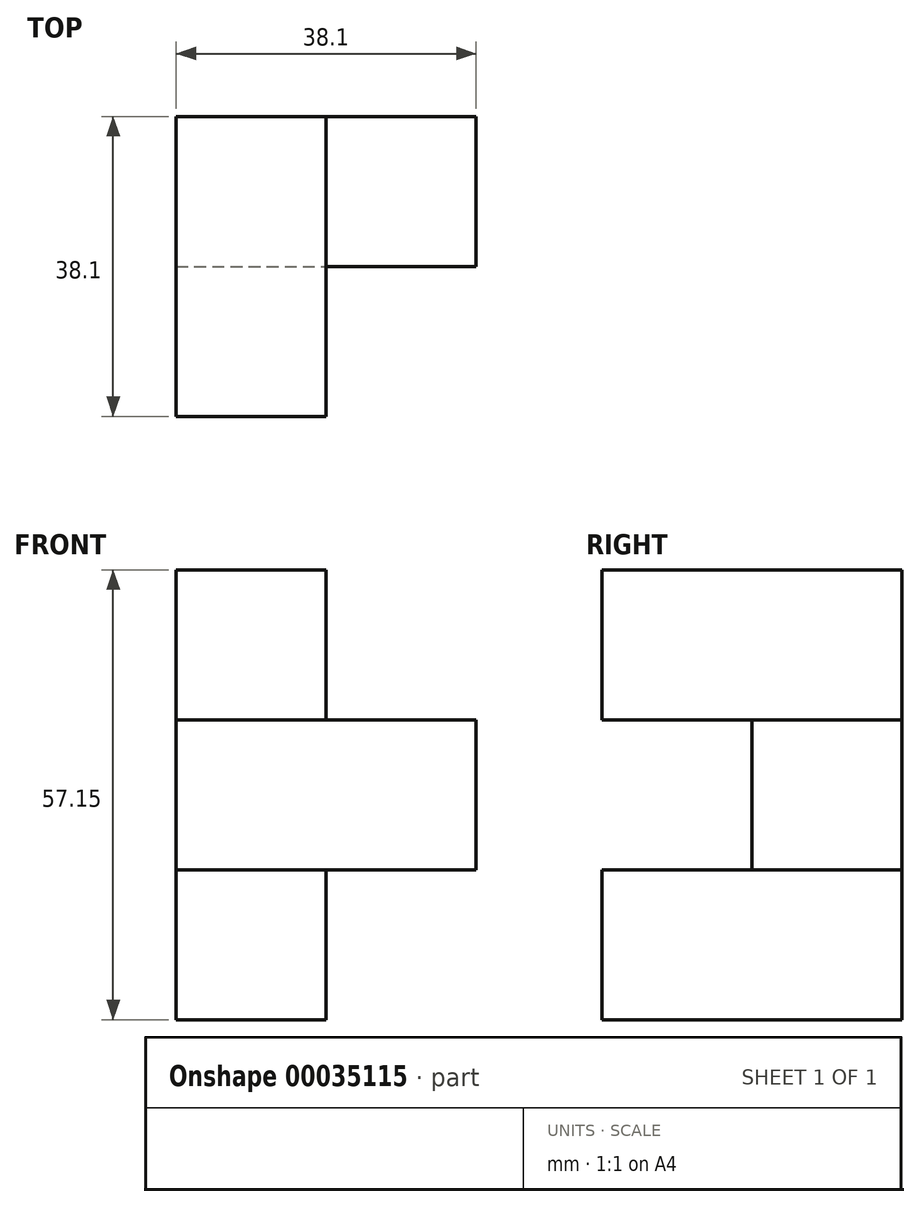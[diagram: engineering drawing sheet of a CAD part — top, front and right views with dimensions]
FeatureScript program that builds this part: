
annotation { "Feature Type Name" : "Feature", "Feature Type Description" : "" }
export const myFeature = defineFeature(function(context is Context, id is Id, definition is map)
    precondition{}
    {
        {
            var Q0;
            Q0=qCreatedBy(makeId("Top.planeOp"),FACE);
            var sketch = newSketch(context, id + "F0", { "sketchPlane" : qUnion([Q0])});
            skLineSegment(sketch, "E0.bottom", {"start": v(0, 0) * mm, "end": v(19.05, 0) * mm});
            skLineSegment(sketch, "E0.top", {"start": v(0, 38.1) * mm, "end": v(19.05, 38.1) * mm});
            skLineSegment(sketch, "E0.left", {"start": v(0, 0) * mm, "end": v(0, 38.1) * mm});
            skLineSegment(sketch, "E0.right", {"start": v(19.05, 0) * mm, "end": v(19.05, 38.1) * mm});
            skSolve(sketch);
        }
        {
            var Q0;
            Q0=makeQuery(id+"F0.imprint","IMPRINT",FACE,{"disambiguationData":[TD([[makeQuery(id+"F0.imprint","IMPRINT",EDGE,{"derivedFrom":sQuery(id+"F0.wireOp",EDGE,"E0.bottom")}),1.0]])]});
            extrude(context, id + "F1", {"entities" : qUnion([Q0]), "depth" : 19.05 * mm});
        }
        {
            var Q0;
            Q0=makeQuery(id+"F1.opExtrude","CAP_FACE",FACE,{"disambiguationData":[OSD([sQuery(id+"F0.wireOp",EDGE,"E0.bottom"),sQuery(id+"F0.wireOp",EDGE,"E0.top"),sQuery(id+"F0.wireOp",EDGE,"E0.left"),sQuery(id+"F0.wireOp",EDGE,"E0.right")])],"isStart":false});
            var sketch = newSketch(context, id + "F2", { "sketchPlane" : qUnion([Q0])});
            skPoint(sketch, "E1.oppositeSnap0", {"position": v(19.05, 19.05) * mm});
            skLineSegment(sketch, "E1.bottom", {"start": v(0, 38.1) * mm, "end": v(38.1, 38.1) * mm});
            skLineSegment(sketch, "E1.top", {"start": v(0, 19.05) * mm, "end": v(38.1, 19.05) * mm});
            skLineSegment(sketch, "E1.left", {"start": v(0, 38.1) * mm, "end": v(0, 19.05) * mm});
            skLineSegment(sketch, "E1.right", {"start": v(38.1, 38.1) * mm, "end": v(38.1, 19.05) * mm});
            skSolve(sketch);
        }
        {
            var Q0;
            {var subQ5=sQuery(id+"F2.wireOp",EDGE,"E1.left");Q0=makeQuery(id+"F2.imprint","IMPRINT",FACE,{"disambiguationData":[TD([[makeQuery(id+"F2.imprint","IMPRINT",EDGE,{"derivedFrom":subQ5}),-1.0]])]});}
            var Q1;
            {var subQ5=sQuery(id+"F2.wireOp",EDGE,"E1.right");Q1=makeQuery(id+"F2.imprint","IMPRINT",FACE,{"disambiguationData":[TD([[makeQuery(id+"F2.imprint","IMPRINT",EDGE,{"derivedFrom":subQ5}),-1.0]])]});}
            extrude(context, id + "F3", {"entities" : qUnion([Q0, Q1]), "operationType" : NewBodyOperationType.ADD, "depth" : 19.05 * mm});
        }
        {
            var Q0;
            Q0=makeQuery(id+"F3.opExtrude","CAP_FACE",FACE,{"disambiguationData":[OSD([sQuery(id+"F2.wireOp",EDGE,"E1.bottom"),sQuery(id+"F2.wireOp",EDGE,"E1.top"),sQuery(id+"F2.wireOp",EDGE,"E1.left"),sQuery(id+"F2.wireOp",EDGE,"E1.right")])],"isStart":false});
            var sketch = newSketch(context, id + "F4", { "sketchPlane" : qUnion([Q0])});
            skPoint(sketch, "E2.oppositeSnap0", {"position": v(19.05, 19.05) * mm});
            skLineSegment(sketch, "E2.bottom", {"start": v(0, 38.1) * mm, "end": v(19.05, 38.1) * mm});
            skLineSegment(sketch, "E2.top", {"start": v(0, 0) * mm, "end": v(19.05, 0) * mm});
            skLineSegment(sketch, "E2.left", {"start": v(0, 38.1) * mm, "end": v(0, 0) * mm});
            skLineSegment(sketch, "E2.right", {"start": v(19.05, 38.1) * mm, "end": v(19.05, 0) * mm});
            skSolve(sketch);
        }
        {
            var Q0;
            Q0 = qSketchRegion(id + "F4", true);
            extrude(context, id + "F5", {"entities" : qUnion([Q0]), "operationType" : NewBodyOperationType.ADD, "depth" : 19.05 * mm});
        }
    });
